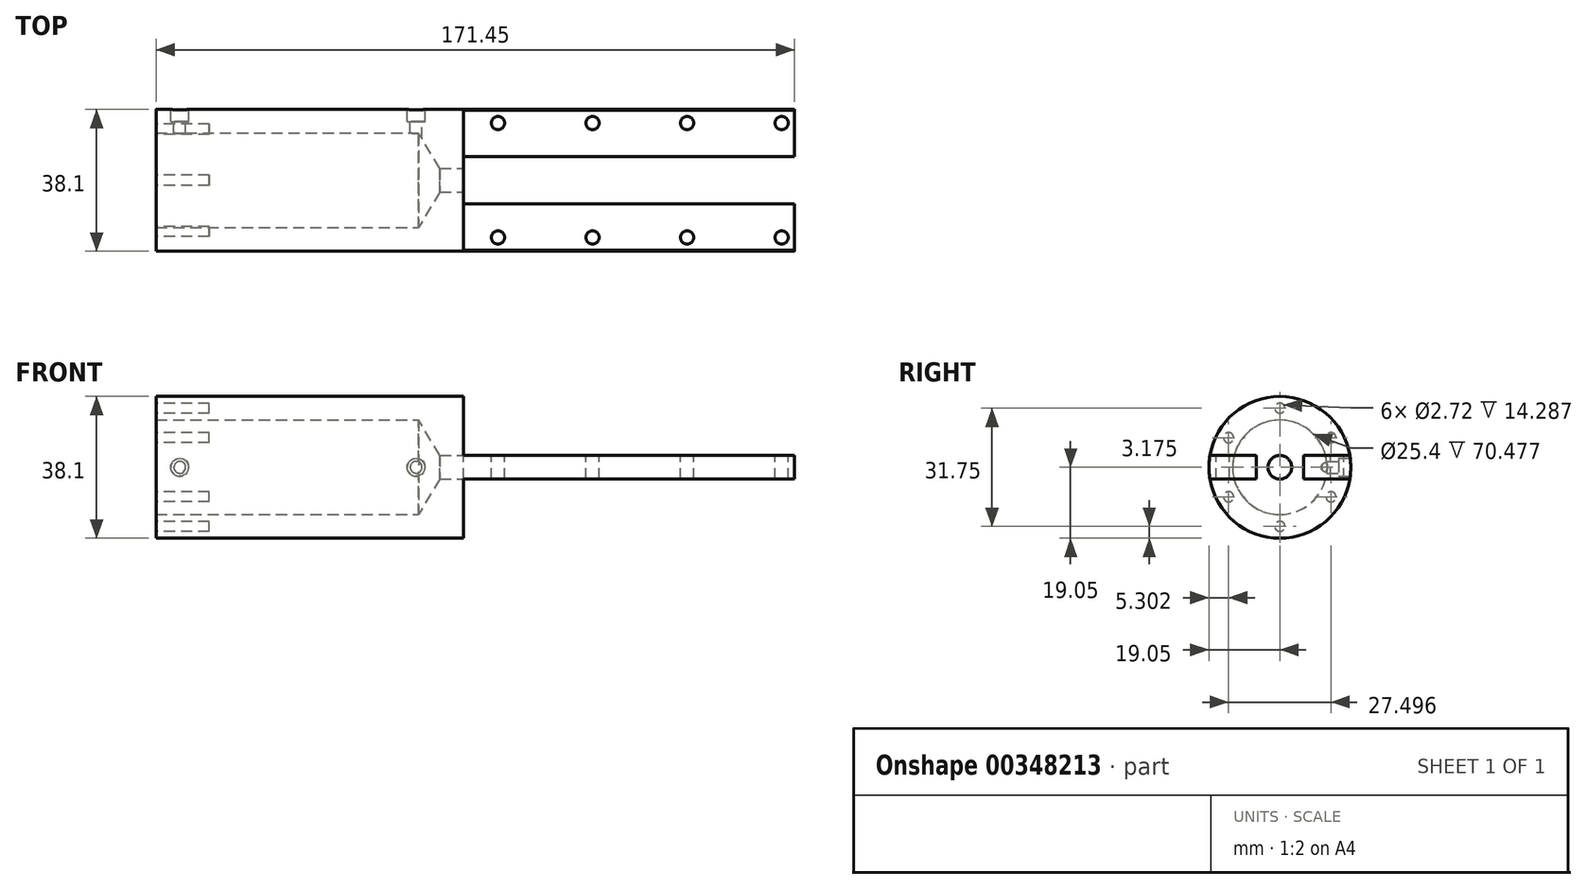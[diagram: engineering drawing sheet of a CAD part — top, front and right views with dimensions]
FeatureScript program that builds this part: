
annotation { "Feature Type Name" : "Feature", "Feature Type Description" : "" }
export const myFeature = defineFeature(function(context is Context, id is Id, definition is map)
    precondition{}
    {
        {
            var Q0;
            Q0=qCreatedBy(makeId("Right.planeOp"),FACE);
            var sketch = newSketch(context, id + "F0", { "sketchPlane" : qUnion([Q0])});
            skCircle(sketch, "E0", {"center": v(0, 0) * mm, "radius": 19.05 * mm});
            skSolve(sketch);
        }
        {
            var Q0;
            Q0=qSketchRegion(id+"F0",true);
            extrude(context, id + "F1", {"entities" : qUnion([Q0]), "depth" : 171.45 * mm});
        }
        {
            var Q0;
            Q0=qCreatedBy(makeId("Front.planeOp"),FACE);
            var sketch = newSketch(context, id + "F2", { "sketchPlane" : qUnion([Q0])});
            skLineSegment(sketch, "E1.bottom", {"start": v(82.55, 3.18) * mm, "end": v(171.45, 3.18) * mm});
            skLineSegment(sketch, "E1.top", {"start": v(82.55, 19.05) * mm, "end": v(171.45, 19.05) * mm});
            skLineSegment(sketch, "E1.left", {"start": v(82.55, 3.18) * mm, "end": v(82.55, 19.05) * mm});
            skLineSegment(sketch, "E1.right", {"start": v(171.45, 3.18) * mm, "end": v(171.45, 19.05) * mm});
            skLineSegment(sketch, "E2.bottom", {"start": v(82.55, -3.18) * mm, "end": v(171.45, -3.18) * mm});
            skLineSegment(sketch, "E2.top", {"start": v(82.55, -19.05) * mm, "end": v(171.45, -19.05) * mm});
            skLineSegment(sketch, "E2.left", {"start": v(82.55, -3.18) * mm, "end": v(82.55, -19.05) * mm});
            skLineSegment(sketch, "E2.right", {"start": v(171.45, -3.18) * mm, "end": v(171.45, -19.05) * mm});
            skLineSegment(sketch, "E3", {"start": v(0, 19.05) * mm, "end": v(171.45, 19.05) * mm, "construction": true});
            skLineSegment(sketch, "E4", {"start": v(171.45, -19.05) * mm, "end": v(0, -19.05) * mm, "construction": true});
            skSolve(sketch);
        }
        {
            var Q0;
            Q0=qSketchRegion(id+"F2",true);
            extrude(context, id + "F3", {"entities" : qUnion([Q0]), "operationType" : NewBodyOperationType.REMOVE, "endBound" : BoundingType.SYMMETRIC, "oppositeDirection" : true, "depth" : 50.8 * mm});
        }
        {
            var Q0;
            Q0=qCreatedBy(makeId("Top.planeOp"),FACE);
            var sketch = newSketch(context, id + "F4", { "sketchPlane" : qUnion([Q0])});
            skLineSegment(sketch, "E5.bottom", {"start": v(171.45, 6.35) * mm, "end": v(82.55, 6.35) * mm});
            skLineSegment(sketch, "E5.top", {"start": v(171.45, -6.35) * mm, "end": v(82.55, -6.35) * mm});
            skLineSegment(sketch, "E5.left", {"start": v(171.45, 6.35) * mm, "end": v(171.45, -6.35) * mm});
            skLineSegment(sketch, "E5.right", {"start": v(82.55, 6.35) * mm, "end": v(82.55, -6.35) * mm});
            skCircle(sketch, "E6", {"center": v(91.82, 15.37) * mm, "radius": 1.78 * mm});
            skCircle(sketch, "E7", {"center": v(91.82, -15.37) * mm, "radius": 1.78 * mm});
            skCircle(sketch, "E8.1.0.0", {"center": v(117.22, 15.37) * mm, "radius": 1.78 * mm});
            skCircle(sketch, "E8.1.0.1", {"center": v(117.22, -15.37) * mm, "radius": 1.78 * mm});
            skCircle(sketch, "E8.2.0.0", {"center": v(142.62, 15.37) * mm, "radius": 1.78 * mm});
            skCircle(sketch, "E8.2.0.1", {"center": v(142.62, -15.37) * mm, "radius": 1.78 * mm});
            skCircle(sketch, "E8.3.0.0", {"center": v(168.02, 15.37) * mm, "radius": 1.78 * mm});
            skCircle(sketch, "E8.3.0.1", {"center": v(168.02, -15.37) * mm, "radius": 1.78 * mm});
            skLineSegment(sketch, "E8.direction1", {"start": v(91.82, 15.37) * mm, "end": v(117.22, 15.37) * mm, "construction": true});
            skSolve(sketch);
        }
        {
            var Q0;
            Q0=qSketchRegion(id+"F4",true);
            extrude(context, id + "F5", {"entities" : qUnion([Q0]), "operationType" : NewBodyOperationType.REMOVE, "endBound" : BoundingType.SYMMETRIC, "oppositeDirection" : true, "depth" : 50.8 * mm});
        }
        {
            var Q0;
            Q0=qCreatedBy(makeId("Top.planeOp"),FACE);
            var sketch = newSketch(context, id + "F6", { "sketchPlane" : qUnion([Q0])});
            skLineSegment(sketch, "E9", {"start": v(0, 0) * mm, "end": v(82.55, 0) * mm});
            skLineSegment(sketch, "E10", {"start": v(82.55, 0) * mm, "end": v(82.55, 3.18) * mm});
            skLineSegment(sketch, "E11", {"start": v(82.55, 3.18) * mm, "end": v(76.2, 3.18) * mm});
            skLineSegment(sketch, "E12", {"start": v(76.2, 3.18) * mm, "end": v(70.48, 12.7) * mm});
            skLineSegment(sketch, "E13", {"start": v(70.48, 12.7) * mm, "end": v(0, 12.7) * mm});
            skLineSegment(sketch, "E14", {"start": v(0, 12.7) * mm, "end": v(0, 0) * mm});
            skSolve(sketch);
        }
        {
            var Q0;
            Q0=qSketchRegion(id+"F6",true);
            var Q1;
            Q1=sQuery(id+"F6.wireOp",EDGE,"E9");
            revolve(context, id + "F7", {"operationType" : NewBodyOperationType.REMOVE, "entities" : qUnion([Q0]), "axis" : qUnion([Q1]), "revolveType" : RevolveType.FULL, "oppositeDirection" : true});
        }
        {
            var Q0;
            Q0=qCreatedBy(makeId("Front.planeOp"),FACE);
            cPlane(context, id + "F8", {"entities" : qUnion([Q0]), "cplaneType" : CPlaneType.OFFSET, "offset" : 19.05 * mm, "oppositeDirection" : true, "width" : 152.4 * mm, "height" : 152.4 * mm});
        }
        {
            var Q0;
            Q0=qCreatedBy(id+"F8.planeOp",FACE);
            var sketch = newSketch(context, id + "F9", { "sketchPlane" : qUnion([Q0])});
            skPoint(sketch, "E15", {"position": v(6.35, 0) * mm});
            skPoint(sketch, "E16", {"position": v(69.85, 0) * mm});
            skSolve(sketch);
        }
        {
            var Q0;
            Q0=sQuery(id+"F9.wireOp",VERTEX,"E15");
            var Q1;
            Q1=sQuery(id+"F9.wireOp",VERTEX,"E16");
            var Q2;
            Q2=makeQuery(id+"F1.opExtrude","SWEPT_BODY",BODY,{"disambiguationData":[OSD([sQuery(id+"F0.wireOp",EDGE,"E0")])]});
            hole(context, id + "F10", {"style" : HoleStyle.C_BORE, "holeDiameter" : 3.17 * mm, "cBoreDiameter" : 4.78 * mm, "cBoreDepth" : 3.17 * mm, "endStyle" : HoleEndStyle.BLIND, "oppositeDirection" : true, "holeDepth" : 7.62 * mm, "locations" : qUnion([Q0, Q1]), "scope" : qUnion([Q2])});
        }
        {
            var Q0;
            Q0=qCreatedBy(makeId("Right.planeOp"),FACE);
            var sketch = newSketch(context, id + "F11", { "sketchPlane" : qUnion([Q0])});
            skCircle(sketch, "E17", {"center": v(0, 0) * mm, "radius": 15.88 * mm, "construction": true});
            skCircle(sketch, "E18", {"center": v(0, 15.88) * mm, "radius": 1.36 * mm});
            skCircle(sketch, "E19.1.0", {"center": v(-13.75, 7.94) * mm, "radius": 1.36 * mm});
            skCircle(sketch, "E19.2.0", {"center": v(-13.75, -7.94) * mm, "radius": 1.36 * mm});
            skCircle(sketch, "E19.3.0", {"center": v(0, -15.88) * mm, "radius": 1.36 * mm});
            skCircle(sketch, "E19.4.0", {"center": v(13.75, -7.94) * mm, "radius": 1.36 * mm});
            skCircle(sketch, "E19.5.0", {"center": v(13.75, 7.94) * mm, "radius": 1.36 * mm});
            skLineSegment(sketch, "E20", {"start": v(0, 0) * mm, "end": v(0, 15.88) * mm, "construction": true});
            skSolve(sketch);
        }
        {
            var Q0;
            Q0=qSketchRegion(id+"F11",true);
            extrude(context, id + "F12", {"entities" : qUnion([Q0]), "operationType" : NewBodyOperationType.REMOVE, "depth" : 14.29 * mm});
        }
    });
